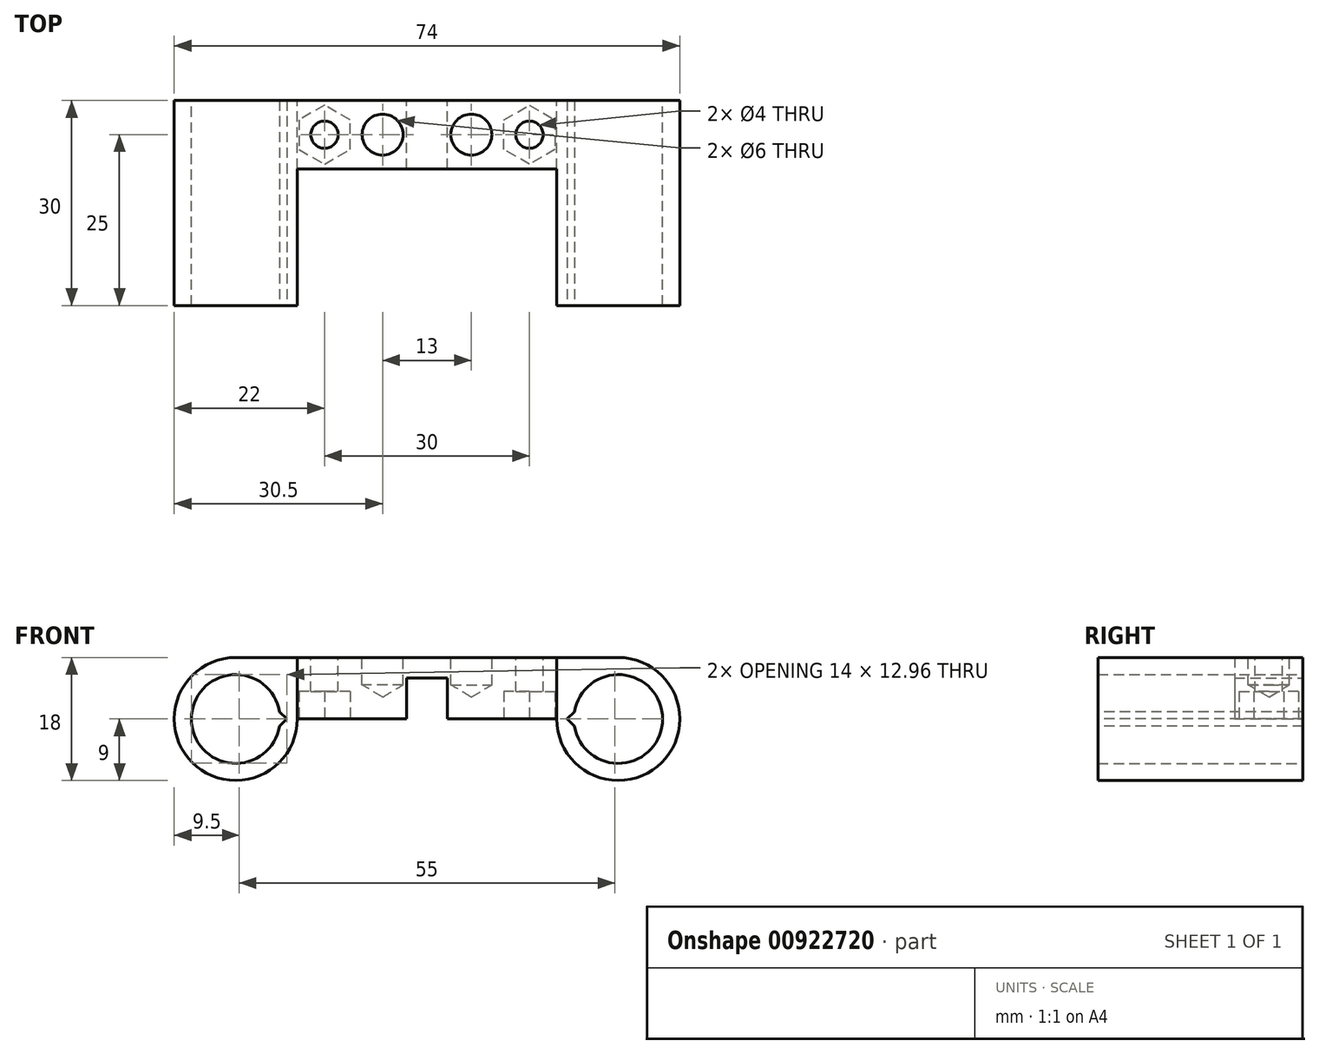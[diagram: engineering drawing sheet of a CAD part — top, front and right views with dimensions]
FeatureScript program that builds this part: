
annotation { "Feature Type Name" : "Feature", "Feature Type Description" : "" }
export const myFeature = defineFeature(function(context is Context, id is Id, definition is map)
    precondition{}
    {
        {
            var Q0;
            Q0=qCreatedBy(makeId("Front.planeOp"),FACE);
            var sketch = newSketch(context, id + "F0", { "sketchPlane" : qUnion([Q0])});
            skLineSegment(sketch, "E0", {"start": v(0, 0) * mm, "end": v(-21.5, 0) * mm});
            skCircle(sketch, "E1", {"center": v(-28, 0) * mm, "radius": 6.5 * mm});
            skCircle(sketch, "E2", {"center": v(-28, 0) * mm, "radius": 9 * mm});
            skLineSegment(sketch, "E3", {"start": v(0, 0) * mm, "end": v(0, 9) * mm});
            skLineSegment(sketch, "E4", {"start": v(0, 9) * mm, "end": v(-28, 9) * mm});
            skSolve(sketch);
        }
        {
            var Q0;
            {var subQ0=sQuery(id+"F0.wireOp",EDGE,"E3");Q0=makeQuery(id+"F0.imprint","IMPRINT",FACE,{"disambiguationData":[TD([[makeQuery(id+"F0.imprint","IMPRINT",EDGE,{"derivedFrom":subQ0}),1.0]])]});}
            var Q1;
            Q1=makeQuery(id+"F0.imprint","IMPRINT",FACE,{"disambiguationData":[TD([[makeQuery(id+"F0.imprint","IMPRINT",EDGE,{"derivedFrom":sQuery(id+"F0.wireOp",EDGE,"E1")}),-1.0]])]});
            extrude(context, id + "F1", {"entities" : qUnion([Q0, Q1]), "depth" : 25 * mm, "offsetDistance" : 25 * mm});
        }
        {
            var Q0;
            Q0=makeQuery(id+"F1.opExtrude","CAP_FACE",FACE,{"disambiguationData":[OSD([sQuery(id+"F0.wireOp",EDGE,"E0"),sQuery(id+"F0.wireOp",EDGE,"E1"),sQuery(id+"F0.wireOp",EDGE,"E2"),sQuery(id+"F0.wireOp",EDGE,"E3"),sQuery(id+"F0.wireOp",EDGE,"E4")])],"isStart":false});
            var sketch = newSketch(context, id + "F2", { "sketchPlane" : qUnion([Q0])});
            skLineSegment(sketch, "E5.bottom", {"start": v(0, 9) * mm, "end": v(-19, 9) * mm});
            skLineSegment(sketch, "E5.top", {"start": v(0, 0) * mm, "end": v(-19, 0) * mm});
            skLineSegment(sketch, "E5.left", {"start": v(0, 9) * mm, "end": v(0, 0) * mm});
            skLineSegment(sketch, "E5.right", {"start": v(-19, 9) * mm, "end": v(-19, 0) * mm});
            skSolve(sketch);
        }
        {
            var Q0;
            Q0=makeQuery(id+"F2.imprint","IMPRINT",FACE,{"disambiguationData":[TD([[makeQuery(id+"F2.imprint","IMPRINT",EDGE,{"derivedFrom":sQuery(id+"F2.wireOp",EDGE,"E5.bottom")}),1.0]])]});
            extrude(context, id + "F3", {"entities" : qUnion([Q0]), "operationType" : NewBodyOperationType.REMOVE, "oppositeDirection" : true, "depth" : 15 * mm, "offsetDistance" : 25 * mm});
        }
        {
            var Q0;
            Q0=makeQuery(id+"F1.opExtrude","SWEPT_FACE",FACE,{"disambiguationData":[OSD([sQuery(id+"F0.wireOp",EDGE,"E4")])]});
            var sketch = newSketch(context, id + "F4", { "sketchPlane" : qUnion([Q0])});
            skCircle(sketch, "E6", {"center": v(-15, -5) * mm, "radius": 2 * mm});
            skSolve(sketch);
        }
        {
            var Q0;
            Q0=makeQuery(id+"F4.imprint","IMPRINT",FACE,{"disambiguationData":[TD([[makeQuery(id+"F4.imprint","IMPRINT",EDGE,{"derivedFrom":sQuery(id+"F4.wireOp",EDGE,"E6")}),1.0]])]});
            extrude(context, id + "F5", {"entities" : qUnion([Q0]), "operationType" : NewBodyOperationType.REMOVE, "endBound" : BoundingType.THROUGH_ALL, "oppositeDirection" : true, "depth" : 25 * mm, "offsetDistance" : 25 * mm});
        }
        {
            var Q0;
            Q0=makeQuery(id+"F1.opExtrude","CAP_FACE",FACE,{"disambiguationData":[OSD([sQuery(id+"F0.wireOp",EDGE,"E0"),sQuery(id+"F0.wireOp",EDGE,"E1"),sQuery(id+"F0.wireOp",EDGE,"E2"),sQuery(id+"F0.wireOp",EDGE,"E3"),sQuery(id+"F0.wireOp",EDGE,"E4")])],"isStart":false});
            var sketch = newSketch(context, id + "F6", { "sketchPlane" : qUnion([Q0])});
            skLineSegment(sketch, "E7", {"start": v(-20.5, 0) * mm, "end": v(-21.58, 1.04) * mm});
            skLineSegment(sketch, "E8", {"start": v(-20.5, 0) * mm, "end": v(-21.58, -1.04) * mm});
            skArc(sketch, "E9", {"start": v(-21.58, 1.04) * mm, "mid": v(-21.5, 0) * mm, "end": v(-21.58, -1.04) * mm});
            skSolve(sketch);
        }
        {
            var Q0;
            Q0 = qSketchRegion(id + "F6", true);
            extrude(context, id + "F7", {"entities" : qUnion([Q0]), "operationType" : NewBodyOperationType.REMOVE, "endBound" : BoundingType.THROUGH_ALL, "oppositeDirection" : true, "depth" : 25 * mm, "offsetDistance" : 25 * mm});
        }
        {
            var Q0;
            Q0=makeQuery(id+"F1.opExtrude","SWEPT_FACE",FACE,{"disambiguationData":[OSD([sQuery(id+"F0.wireOp",EDGE,"E0")])]});
            var sketch = newSketch(context, id + "F8", { "sketchPlane" : qUnion([Q0])});
            skCircle(sketch, "E10", {"center": v(-15, 5) * mm, "radius": 3.75 * mm});
            skCircle(sketch, "E11.cCircle", {"center": v(-15, 5) * mm, "radius": 3.75 * mm, "construction": true});
            skLineSegment(sketch, "E11.0", {"start": v(-11.25, 7.17) * mm, "end": v(-11.25, 2.83) * mm});
            skLineSegment(sketch, "E11.1", {"start": v(-11.25, 2.83) * mm, "end": v(-15, 0.67) * mm});
            skLineSegment(sketch, "E11.2", {"start": v(-15, 0.67) * mm, "end": v(-18.75, 2.83) * mm});
            skLineSegment(sketch, "E11.3", {"start": v(-18.75, 2.83) * mm, "end": v(-18.75, 7.17) * mm});
            skLineSegment(sketch, "E11.4", {"start": v(-18.75, 7.17) * mm, "end": v(-15, 9.33) * mm});
            skLineSegment(sketch, "E11.5", {"start": v(-15, 9.33) * mm, "end": v(-11.25, 7.17) * mm});
            skPoint(sketch, "E11.0.midPoint", {"position": v(-11.25, 5) * mm});
            skSolve(sketch);
        }
        {
            var Q0;
            Q0 = qSketchRegion(id + "F8", true);
            extrude(context, id + "F9", {"entities" : qUnion([Q0]), "operationType" : NewBodyOperationType.REMOVE, "oppositeDirection" : true, "depth" : 4 * mm, "offsetDistance" : 25 * mm});
        }
        {
            var Q0;
            Q0=makeQuery(id+"F1.opExtrude","CAP_FACE",FACE,{"disambiguationData":[OSD([sQuery(id+"F0.wireOp",EDGE,"E0"),sQuery(id+"F0.wireOp",EDGE,"E1"),sQuery(id+"F0.wireOp",EDGE,"E2"),sQuery(id+"F0.wireOp",EDGE,"E3"),sQuery(id+"F0.wireOp",EDGE,"E4")])],"isStart":false});
            extrude(context, id + "F10", {"entities" : qUnion([Q0]), "operationType" : NewBodyOperationType.ADD, "depth" : 5 * mm, "offsetDistance" : 25 * mm});
        }
        {
            var Q0;
            {var subQ0=sQuery(id+"F0.wireOp",EDGE,"E4");Q0=makeQuery(id+"F10.boolean.opBoolean","MERGE",FACE,{"derivedFrom":[makeQuery(id+"F1.opExtrude","SWEPT_FACE",FACE,{"disambiguationData":[OSD([subQ0])]}),makeQuery(id+"F10.opExtrude","SWEPT_FACE",FACE,{"disambiguationData":[OSD([subQ0])]})]});}
            var sketch = newSketch(context, id + "F11", { "sketchPlane" : qUnion([Q0])});
            skLineSegment(sketch, "E12", {"start": v(0, -5) * mm, "end": v(-13, -5) * mm});
            skPoint(sketch, "E13", {"position": v(-6.5, -5) * mm});
            skSolve(sketch);
        }
        {
            var Q0;
            Q0=sQuery(id+"F11.wireOp",VERTEX,"E13");
            var Q1;
            Q1=makeQuery(id+"F1.opExtrude","SWEPT_BODY",BODY,{"disambiguationData":[OSD([sQuery(id+"F0.wireOp",EDGE,"E0"),sQuery(id+"F0.wireOp",EDGE,"E1"),sQuery(id+"F0.wireOp",EDGE,"E2"),sQuery(id+"F0.wireOp",EDGE,"E3"),sQuery(id+"F0.wireOp",EDGE,"E4")])]});
            hole(context, id + "F12", {"style" : HoleStyle.SIMPLE, "endStyle" : HoleEndStyle.BLIND, "holeDiameter" : 6 * mm, "majorDiameter" : 5 * mm, "holeDepth" : 4 * mm, "isTappedThrough" : true, "tappedDepth" : 12 * mm, "tapClearance" : 3, "locations" : qUnion([Q0]), "scope" : qUnion([Q1])});
        }
        {
            var Q0;
            Q0=makeQuery(id+"F1.opExtrude","CAP_FACE",FACE,{"disambiguationData":[OSD([sQuery(id+"F0.wireOp",EDGE,"E0"),sQuery(id+"F0.wireOp",EDGE,"E1"),sQuery(id+"F0.wireOp",EDGE,"E2"),sQuery(id+"F0.wireOp",EDGE,"E3"),sQuery(id+"F0.wireOp",EDGE,"E4")])],"isStart":true});
            var sketch = newSketch(context, id + "F13", { "sketchPlane" : qUnion([Q0])});
            skLineSegment(sketch, "E14.bottom", {"start": v(0, 0) * mm, "end": v(3, 0) * mm});
            skLineSegment(sketch, "E14.top", {"start": v(0, 6) * mm, "end": v(3, 6) * mm});
            skLineSegment(sketch, "E14.left", {"start": v(0, 0) * mm, "end": v(0, 6) * mm});
            skLineSegment(sketch, "E14.right", {"start": v(3, 0) * mm, "end": v(3, 6) * mm});
            skSolve(sketch);
        }
        {
            var Q0;
            Q0 = qSketchRegion(id + "F13", true);
            extrude(context, id + "F14", {"entities" : qUnion([Q0]), "operationType" : NewBodyOperationType.REMOVE, "endBound" : BoundingType.THROUGH_ALL, "oppositeDirection" : true, "depth" : 25 * mm, "offsetDistance" : 25 * mm});
        }
        {
            var Q0;
            Q0=makeQuery(id+"F1.opExtrude","SWEPT_BODY",BODY,{"disambiguationData":[OSD([sQuery(id+"F0.wireOp",EDGE,"E0"),sQuery(id+"F0.wireOp",EDGE,"E1"),sQuery(id+"F0.wireOp",EDGE,"E2"),sQuery(id+"F0.wireOp",EDGE,"E3"),sQuery(id+"F0.wireOp",EDGE,"E4")])]});
            var Q1;
            Q1=qCreatedBy(makeId("Right.planeOp"),FACE);
            mirror(context, id + "F15", {"operationType" : NewBodyOperationType.ADD, "entities" : qUnion([Q0]), "mirrorPlane" : qUnion([Q1])});
        }
    });
